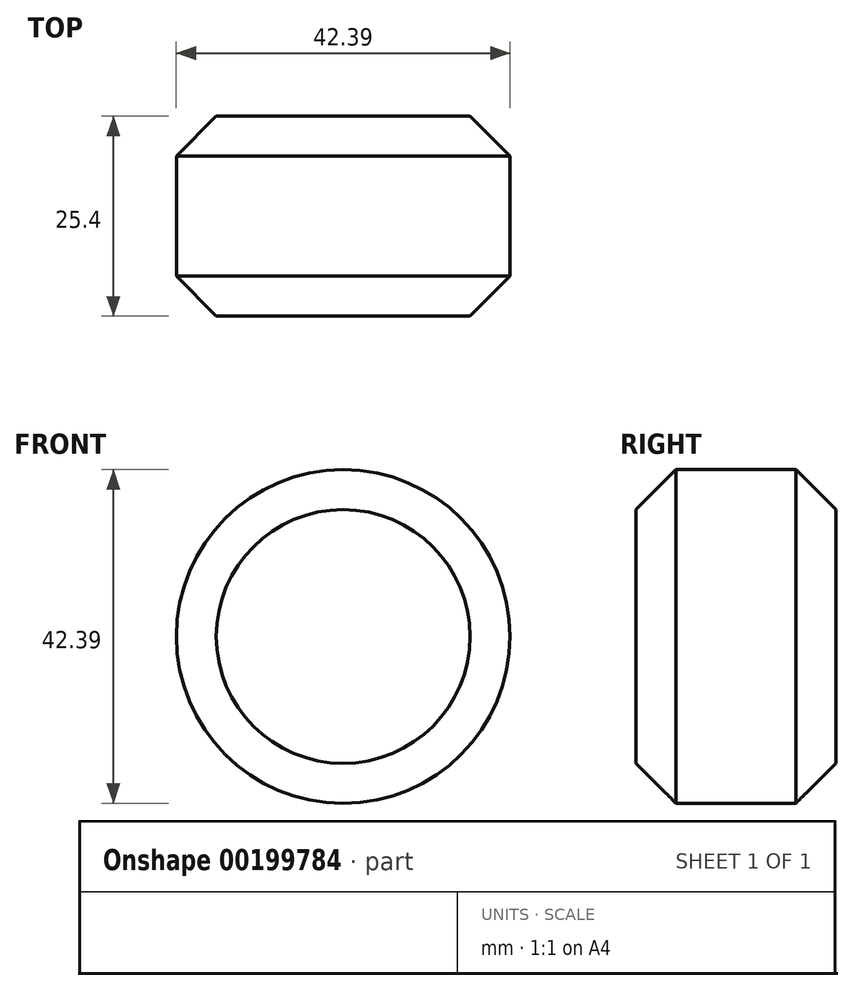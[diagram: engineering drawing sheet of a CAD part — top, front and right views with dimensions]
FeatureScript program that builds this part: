
annotation { "Feature Type Name" : "Feature", "Feature Type Description" : "" }
export const myFeature = defineFeature(function(context is Context, id is Id, definition is map)
    precondition{}
    {
        {
            var Q0;
            Q0=qCreatedBy(makeId("Front.planeOp"),FACE);
            var sketch = newSketch(context, id + "F0", { "sketchPlane" : qUnion([Q0])});
            skCircle(sketch, "E0", {"center": v(-27.95, 20.4) * mm, "radius": 21.2 * mm});
            skSolve(sketch);
        }
        {
            var Q0;
            Q0 = qSketchRegion(id + "F0", true);
            extrude(context, id + "F1", {"entities" : qUnion([Q0]), "depth" : 25.4 * mm});
        }
        {
            var Q0;
            Q0=makeQuery(id+"F1.opExtrude","SWEPT_FACE",FACE,{"disambiguationData":[OSD([sQuery(id+"F0.wireOp",EDGE,"E0")])]});
            chamfer(context, id + "F2", {"entities" : qUnion([Q0]), "width" : 5.08 * mm, "tangentPropagation" : true});
        }
    });
